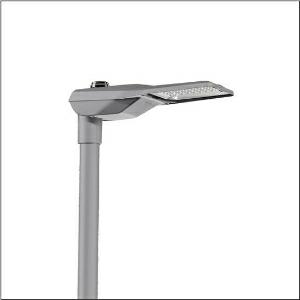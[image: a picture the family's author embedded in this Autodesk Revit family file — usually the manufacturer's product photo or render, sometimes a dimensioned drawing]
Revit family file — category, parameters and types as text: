
# Revit family: streetlight_sl_21_mini___stw1_0a_5xe6e47n08jb_ac66
name_source: partatom
category: Lighting Fixtures
units: mm (PartAtom-declared; Revit-internal decimal feet)

## family parameters
Cut with Voids When Loaded = No
Host = Face
Light Source = No
Part Type = Normal
Room Calculation Point = No
Round Connector Dimension = Use Diameter
Shared = No

## types (1)
- --- (1 x LED, 13390 lm, 87.3 W, 4000K)
    Apparent Load = 87 VA
    CIE Flux Codes = 39 75 98 100 100
    Color Rendering = 70
    Color Temperature = 4000K
    Default Elevation = 1800 mm
    Description = Streetlight SL 21 mini, mast luminaire, primary light control with lens, of PMMA, primary optical cover: cover, of toughened safety glass, transparent, light distribution: STW1.0a, light emission: direct distribution, primary light characteristic: asymmetric, installation type: side-entry, LED, 3G 2.5mm², High Power LED, rated luminous flux: 13.390lm, luminous efficacy: 153lm/W, light colour: 740, colour temperature: 4000K, control gear: NEMA (7pin), control: overheat protection, pre-setting: linear dimming characteristic, constant luminous flux control, time-dependent luminous flux control, flexible luminous flux parameterisation, mains connection: 230..240V, AC, 50/60Hz, connection cable pre-assembled, cable length: 10,5m, wiring characteristics: H05VV-F, start of lifetime: 87W, end of service life: 90W, reduction: 40W, luminaire housing, of diecast aluminium (EN AC-44300), powder-coated, SITECO metallic grey (DB 702S), corrosivity category C5 high according to DIN EN ISO 12944, multi-level sealing system, sealing non-destructively replaceable, inclination adjustable: 0°, 5°, 10°, 15°, length: 628mm, width: 235mm, height: 110mm, spigot size: 42mm (side-entry), mounting height: 4..8m, protection rating (complete): IP66, insulation class (complete): insulation class I (protective earthing), certification: CE, ENEC, ENEC+, VDE, impact resistance: IK10, permissible operating ambient temperature for outdoor applications: -40..+50°C, standard-compliant lighting for roads and squares, packaging unit: 1 piece

Light Distribution: STW1.0a
    Height = 110 mm
    Lamp = 1 x LED
    Lamp Light Flux = 13390 lm
    Lamp Power = 87.3 W
    Lamp count = 1
    Length = 625 mm
    Luminous efficacy = 153 lm/W
    Manufacturer = Siteco
    ModVariant = No
    Model = 5XE6E47N08JB
    Number of Poles = 1
    OnlyDefault = Yes
    Power Factor = 1
    Product Name = Streetlight SL 21 mini | STW1.0a
    Product group = mast luminaire | pylon top
    ProductGroupID = 6100
    Protection Class = Protection class I
    Protection Degree = IP 66
    RLX_Detail_Level = 1
    RLX_Emergency_Light_Flux = 0 lm
    RLX_Emergency_Type = 0
    RLX_Emergency_Type_DB = No
    RlxData = <blob elided: 26165 chars, md5=cb4dbffb>
    Socket = socket
    Standby Power = 0 W
    System Light Flux = 13390 lm
    System Power = 87 W
    Type Comments = factory setting: luminous flux: 100 % | dim-lin: 254 | 915 mA
    Type Image = l_1294379.jpg
    URL = http://relux.com
    VarID = @adj_134467
    Voltage = 0 V
    Weight = 0.00 kg
    Width = 234 mm

## geometry (parser evidence)
native form markers: Blend x4, Sweep x11
no freeform markers — native parametric forms only
